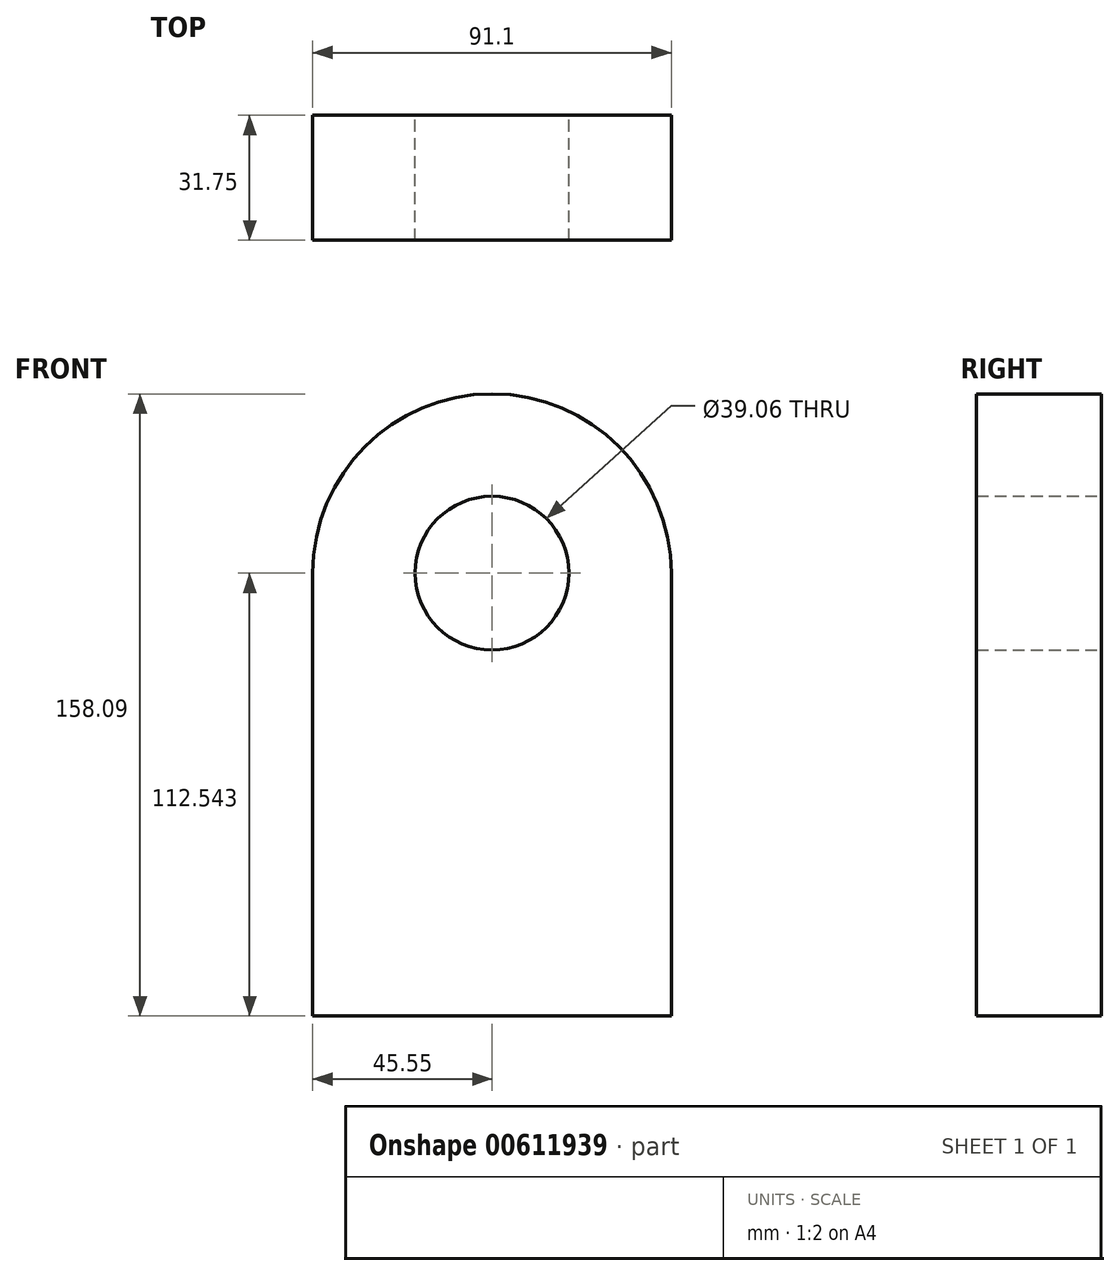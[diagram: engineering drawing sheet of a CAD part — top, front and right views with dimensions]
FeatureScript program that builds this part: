
annotation { "Feature Type Name" : "Feature", "Feature Type Description" : "" }
export const myFeature = defineFeature(function(context is Context, id is Id, definition is map)
    precondition{}
    {
        {
            var Q0;
            Q0=qCreatedBy(makeId("Front.planeOp"),FACE);
            var sketch = newSketch(context, id + "F0", { "sketchPlane" : qUnion([Q0])});
            skLineSegment(sketch, "E0.bottom", {"start": v(45.55, -56.27) * mm, "end": v(-45.55, -56.27) * mm});
            skLineSegment(sketch, "E0.left", {"start": v(45.55, -56.27) * mm, "end": v(45.55, 56.27) * mm});
            skLineSegment(sketch, "E0.right", {"start": v(-45.55, -56.27) * mm, "end": v(-45.55, 56.27) * mm});
            skPoint(sketch, "E0.middle", {"position": v(0, 0) * mm});
            skArc(sketch, "E1", {"start": v(45.55, 56.27) * mm, "mid": v(0, 101.82) * mm, "end": v(-45.55, 56.27) * mm});
            skCircle(sketch, "E2", {"center": v(0, 56.27) * mm, "radius": 19.53 * mm});
            skSolve(sketch);
        }
        {
            var Q0;
            Q0=makeQuery(id+"F0.imprint","IMPRINT",FACE,{"disambiguationData":[TD([[makeQuery(id+"F0.imprint","IMPRINT",EDGE,{"derivedFrom":sQuery(id+"F0.wireOp",EDGE,"E0.bottom")}),-1.0]])]});
            extrude(context, id + "F1", {"entities" : qUnion([Q0]), "depth" : 31.75 * mm, "offsetDistance" : 25.4 * mm});
        }
    });
